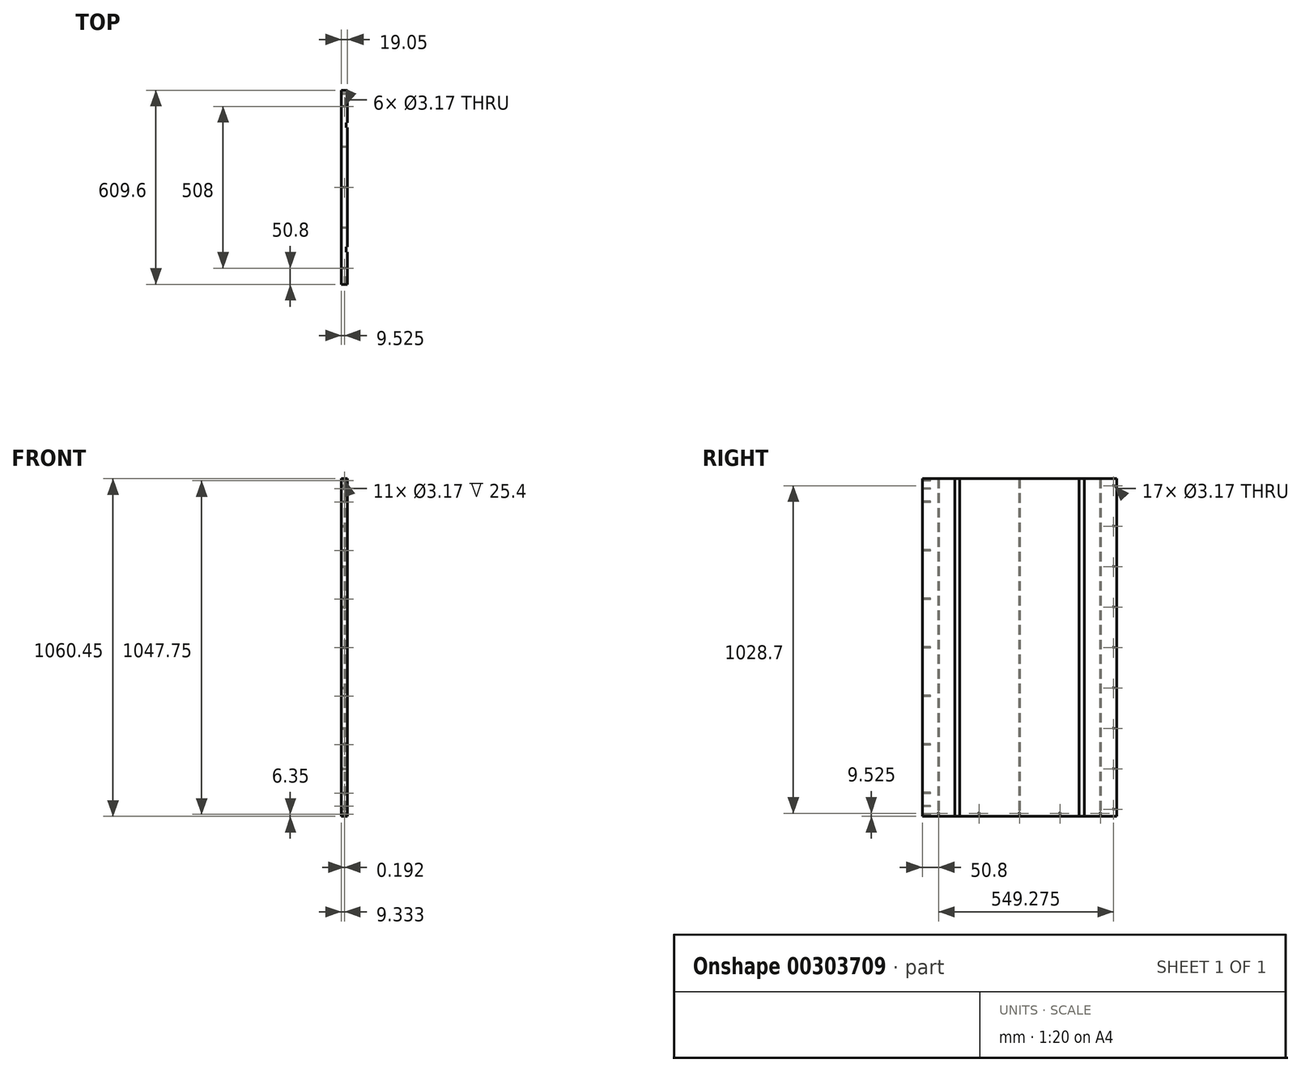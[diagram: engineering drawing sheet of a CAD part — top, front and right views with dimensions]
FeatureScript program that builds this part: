
annotation { "Feature Type Name" : "Feature", "Feature Type Description" : "" }
export const myFeature = defineFeature(function(context is Context, id is Id, definition is map)
    precondition{}
    {
        {
            var Q0;
            Q0=qCreatedBy(makeId("Front.planeOp"),FACE);
            var sketch = newSketch(context, id + "F0", { "sketchPlane" : qUnion([Q0])});
            skLineSegment(sketch, "E0.bottom", {"start": v(0, 0) * mm, "end": v(19.05, 0) * mm});
            skLineSegment(sketch, "E0.top", {"start": v(0, 1060.45) * mm, "end": v(19.05, 1060.45) * mm});
            skLineSegment(sketch, "E0.left", {"start": v(0, 0) * mm, "end": v(0, 1060.45) * mm});
            skLineSegment(sketch, "E0.right", {"start": v(19.05, 0) * mm, "end": v(19.05, 1060.45) * mm});
            skSolve(sketch);
        }
        {
            var Q0;
            Q0=qSketchRegion(id+"F0",true);
            extrude(context, id + "F1", {"entities" : qUnion([Q0]), "oppositeDirection" : true, "depth" : 609.6 * mm});
        }
        {
            var Q0;
            Q0=qCreatedBy(makeId("Right.planeOp"),FACE);
            var sketch = newSketch(context, id + "F2", { "sketchPlane" : qUnion([Q0])});
            skCircle(sketch, "E1", {"center": v(50.8, 9.53) * mm, "radius": 1.59 * mm});
            skCircle(sketch, "E2.1.0.0", {"center": v(177.8, 9.53) * mm, "radius": 1.59 * mm});
            skCircle(sketch, "E2.2.0.0", {"center": v(304.8, 9.53) * mm, "radius": 1.59 * mm});
            skCircle(sketch, "E2.3.0.0", {"center": v(431.8, 9.53) * mm, "radius": 1.59 * mm});
            skCircle(sketch, "E2.4.0.0", {"center": v(558.8, 9.53) * mm, "radius": 1.59 * mm});
            skLineSegment(sketch, "E2.direction1", {"start": v(50.8, 9.53) * mm, "end": v(177.8, 9.53) * mm, "construction": true});
            skSolve(sketch);
        }
        {
            var Q0;
            Q0=qSketchRegion(id+"F2",true);
            extrude(context, id + "F3", {"entities" : qUnion([Q0]), "operationType" : NewBodyOperationType.REMOVE, "endBound" : BoundingType.THROUGH_ALL, "depth" : 25.4 * mm});
        }
        {
            var Q0;
            Q0=qCreatedBy(makeId("Front.planeOp"),FACE);
            var sketch = newSketch(context, id + "F4", { "sketchPlane" : qUnion([Q0])});
            skCircle(sketch, "E3", {"center": v(9.53, 1054.1) * mm, "radius": 1.59 * mm});
            skCircle(sketch, "E4.1.0.0", {"center": v(9.33, 1028.7) * mm, "radius": 1.59 * mm});
            skLineSegment(sketch, "E4.direction1", {"start": v(9.53, 1054.1) * mm, "end": v(9.33, 1028.7) * mm, "construction": true});
            skSolve(sketch);
        }
        {
            var Q0;
            Q0=qSketchRegion(id+"F4",true);
            extrude(context, id + "F5", {"entities" : qUnion([Q0]), "operationType" : NewBodyOperationType.REMOVE, "oppositeDirection" : true, "depth" : 25.4 * mm});
        }
        {
            var Q0;
            Q0=qCreatedBy(makeId("Front.planeOp"),FACE);
            var sketch = newSketch(context, id + "F6", { "sketchPlane" : qUnion([Q0])});
            skCircle(sketch, "E5", {"center": v(9.53, 6.35) * mm, "radius": 1.59 * mm});
            skCircle(sketch, "E6.0.1.0", {"center": v(9.53, 31.75) * mm, "radius": 1.59 * mm});
            skLineSegment(sketch, "E6.direction1", {"start": v(9.53, 6.35) * mm, "end": v(9.52, 6.35) * mm});
            skLineSegment(sketch, "E6.direction2", {"start": v(9.53, 6.35) * mm, "end": v(9.53, 31.75) * mm, "construction": true});
            skSolve(sketch);
        }
        {
            var Q0;
            Q0=qSketchRegion(id+"F6",true);
            extrude(context, id + "F7", {"entities" : qUnion([Q0]), "operationType" : NewBodyOperationType.REMOVE, "oppositeDirection" : true, "depth" : 25.4 * mm});
        }
        {
            var Q0;
            Q0=qCreatedBy(makeId("Front.planeOp"),FACE);
            var sketch = newSketch(context, id + "F8", { "sketchPlane" : qUnion([Q0])});
            skCircle(sketch, "E7", {"center": v(9.53, 987.43) * mm, "radius": 1.59 * mm});
            skCircle(sketch, "E8.0.1.0", {"center": v(9.53, 835.03) * mm, "radius": 1.59 * mm});
            skCircle(sketch, "E8.0.2.0", {"center": v(9.53, 682.63) * mm, "radius": 1.59 * mm});
            skCircle(sketch, "E8.0.3.0", {"center": v(9.53, 530.23) * mm, "radius": 1.59 * mm});
            skCircle(sketch, "E8.0.4.0", {"center": v(9.53, 377.83) * mm, "radius": 1.59 * mm});
            skCircle(sketch, "E8.0.5.0", {"center": v(9.53, 225.43) * mm, "radius": 1.59 * mm});
            skCircle(sketch, "E8.0.6.0", {"center": v(9.53, 73.03) * mm, "radius": 1.59 * mm});
            skLineSegment(sketch, "E8.direction1", {"start": v(9.53, 987.43) * mm, "end": v(34.92, 987.43) * mm, "construction": true});
            skLineSegment(sketch, "E8.direction2", {"start": v(9.53, 987.43) * mm, "end": v(9.53, 835.03) * mm, "construction": true});
            skSolve(sketch);
        }
        {
            var Q0;
            Q0=qSketchRegion(id+"F8",true);
            extrude(context, id + "F9", {"entities" : qUnion([Q0]), "operationType" : NewBodyOperationType.REMOVE, "oppositeDirection" : true, "depth" : 25.4 * mm});
        }
        {
            var Q0;
            Q0=makeQuery(id+"F1.opExtrude","SWEPT_FACE",FACE,{"disambiguationData":[OSD([sQuery(id+"F0.wireOp",EDGE,"E0.right")])]});
            var sketch = newSketch(context, id + "F10", { "sketchPlane" : qUnion([Q0])});
            skCircle(sketch, "E9", {"center": v(600.07, 1038.23) * mm, "radius": 1.59 * mm});
            skCircle(sketch, "E10.0.1.0", {"center": v(600.07, 911.23) * mm, "radius": 1.59 * mm});
            skCircle(sketch, "E10.0.2.0", {"center": v(600.07, 784.23) * mm, "radius": 1.59 * mm});
            skCircle(sketch, "E10.0.3.0", {"center": v(600.07, 657.23) * mm, "radius": 1.59 * mm});
            skCircle(sketch, "E10.0.4.0", {"center": v(600.07, 530.23) * mm, "radius": 1.59 * mm});
            skCircle(sketch, "E10.0.5.0", {"center": v(600.07, 403.23) * mm, "radius": 1.59 * mm});
            skCircle(sketch, "E10.0.6.0", {"center": v(600.07, 276.22) * mm, "radius": 1.59 * mm});
            skCircle(sketch, "E10.0.7.0", {"center": v(600.07, 149.22) * mm, "radius": 1.59 * mm});
            skCircle(sketch, "E10.0.8.0", {"center": v(600.07, 22.22) * mm, "radius": 1.59 * mm});
            skLineSegment(sketch, "E10.direction1", {"start": v(600.07, 1038.23) * mm, "end": v(625.47, 1038.23) * mm, "construction": true});
            skLineSegment(sketch, "E10.direction2", {"start": v(600.07, 1038.23) * mm, "end": v(600.07, 911.22) * mm, "construction": true});
            skSolve(sketch);
        }
        {
            var Q0;
            Q0=qSketchRegion(id+"F10",true);
            extrude(context, id + "F11", {"entities" : qUnion([Q0]), "operationType" : NewBodyOperationType.REMOVE, "endBound" : BoundingType.THROUGH_ALL, "oppositeDirection" : true, "depth" : 25.4 * mm});
        }
        {
            var Q0;
            Q0=makeQuery(id+"F1.opExtrude","SWEPT_FACE",FACE,{"disambiguationData":[OSD([sQuery(id+"F0.wireOp",EDGE,"E0.bottom")])]});
            var sketch = newSketch(context, id + "F12", { "sketchPlane" : qUnion([Q0])});
            skLineSegment(sketch, "E11", {"start": v(19.05, 0) * mm, "end": v(19.05, -101.6) * mm});
            skLineSegment(sketch, "E12.bottom", {"start": v(19.05, -101.6) * mm, "end": v(14.22, -101.6) * mm});
            skLineSegment(sketch, "E12.top", {"start": v(19.05, -117.48) * mm, "end": v(14.22, -117.48) * mm});
            skLineSegment(sketch, "E12.left", {"start": v(19.05, -101.6) * mm, "end": v(19.05, -117.48) * mm});
            skLineSegment(sketch, "E12.right", {"start": v(14.22, -101.6) * mm, "end": v(14.22, -117.48) * mm});
            skSolve(sketch);
        }
        {
            var Q0;
            Q0=makeQuery(id+"F12.imprint","IMPRINT",FACE,{"disambiguationData":[TD([[makeQuery(id+"F12.imprint","IMPRINT",EDGE,{"derivedFrom":sQuery(id+"F12.wireOp",EDGE,"E12.bottom")}),1.0]])]});
            extrude(context, id + "F13", {"entities" : qUnion([Q0]), "operationType" : NewBodyOperationType.REMOVE, "endBound" : BoundingType.THROUGH_ALL, "oppositeDirection" : true, "depth" : 25.4 * mm, "offsetDistance" : 25.4 * mm});
        }
        {
            var Q0;
            Q0=makeQuery(id+"F1.opExtrude","SWEPT_FACE",FACE,{"disambiguationData":[OSD([sQuery(id+"F0.wireOp",EDGE,"E0.bottom")])]});
            var sketch = newSketch(context, id + "F14", { "sketchPlane" : qUnion([Q0])});
            skLineSegment(sketch, "E13", {"start": v(19.05, -609.6) * mm, "end": v(19.05, -508) * mm});
            skLineSegment(sketch, "E14.bottom", {"start": v(19.05, -508) * mm, "end": v(14.22, -508) * mm});
            skLineSegment(sketch, "E14.top", {"start": v(19.05, -492.13) * mm, "end": v(14.22, -492.13) * mm});
            skLineSegment(sketch, "E14.left", {"start": v(19.05, -508) * mm, "end": v(19.05, -492.13) * mm});
            skLineSegment(sketch, "E14.right", {"start": v(14.22, -508) * mm, "end": v(14.22, -492.13) * mm});
            skSolve(sketch);
        }
        {
            var Q0;
            Q0=makeQuery(id+"F14.imprint","IMPRINT",FACE,{"disambiguationData":[TD([[makeQuery(id+"F14.imprint","IMPRINT",EDGE,{"derivedFrom":sQuery(id+"F14.wireOp",EDGE,"E14.bottom")}),-1.0]])]});
            extrude(context, id + "F15", {"entities" : qUnion([Q0]), "operationType" : NewBodyOperationType.REMOVE, "endBound" : BoundingType.THROUGH_ALL, "oppositeDirection" : true, "depth" : 25.4 * mm, "offsetDistance" : 25.4 * mm});
        }
        {
            var Q0;
            Q0=qCreatedBy(makeId("Top.planeOp"),FACE);
            var sketch = newSketch(context, id + "F16", { "sketchPlane" : qUnion([Q0])});
            skCircle(sketch, "E15", {"center": v(9.53, 50.8) * mm, "radius": 1.59 * mm});
            skCircle(sketch, "E16.0.1.0", {"center": v(9.53, 304.8) * mm, "radius": 1.59 * mm});
            skCircle(sketch, "E16.0.2.0", {"center": v(9.53, 558.8) * mm, "radius": 1.59 * mm});
            skLineSegment(sketch, "E16.direction1", {"start": v(9.53, 50.8) * mm, "end": v(34.92, 50.8) * mm, "construction": true});
            skLineSegment(sketch, "E16.direction2", {"start": v(9.53, 50.8) * mm, "end": v(9.53, 304.8) * mm, "construction": true});
            skSolve(sketch);
        }
        {
            var Q0;
            Q0 = qSketchRegion(id + "F16", true);
            extrude(context, id + "F17", {"entities" : qUnion([Q0]), "operationType" : NewBodyOperationType.REMOVE, "endBound" : BoundingType.THROUGH_ALL, "depth" : 25.4 * mm, "offsetDistance" : 25.4 * mm});
        }
    });
